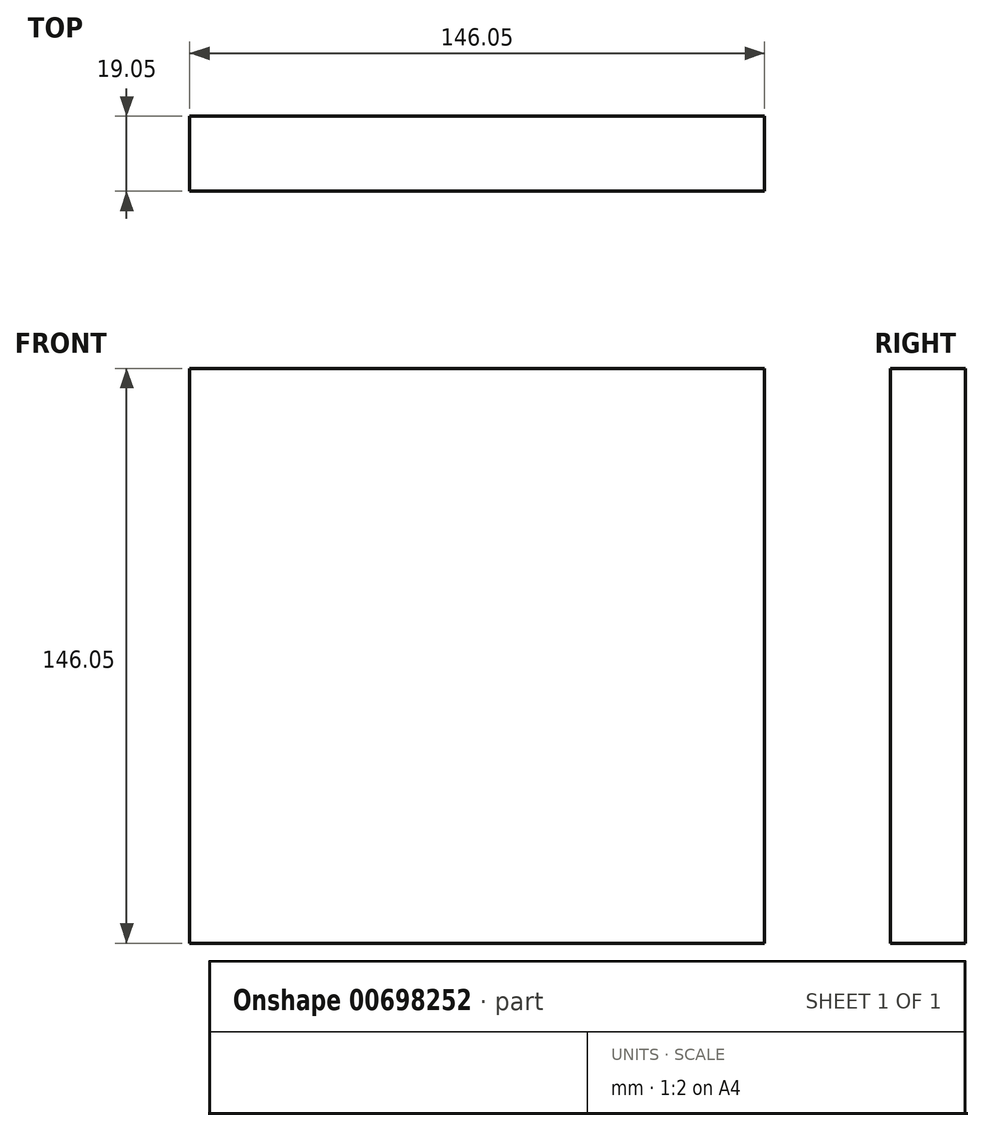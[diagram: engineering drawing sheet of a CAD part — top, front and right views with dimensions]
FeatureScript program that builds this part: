
annotation { "Feature Type Name" : "Feature", "Feature Type Description" : "" }
export const myFeature = defineFeature(function(context is Context, id is Id, definition is map)
    precondition{}
    {
        {
            var Q0;
            Q0=qCreatedBy(makeId("Front.planeOp"),FACE);
            var sketch = newSketch(context, id + "F0", { "sketchPlane" : qUnion([Q0])});
            skLineSegment(sketch, "E0.bottom", {"start": v(-72.42, -55.88) * mm, "end": v(73.63, -55.88) * mm});
            skLineSegment(sketch, "E0.top", {"start": v(-72.42, 90.17) * mm, "end": v(73.63, 90.17) * mm});
            skLineSegment(sketch, "E0.left", {"start": v(-72.42, -55.88) * mm, "end": v(-72.42, 90.17) * mm});
            skLineSegment(sketch, "E0.right", {"start": v(73.63, -55.88) * mm, "end": v(73.63, 90.17) * mm});
            skSolve(sketch);
        }
        {
            var Q0;
            Q0 = qSketchRegion(id + "F0", true);
            extrude(context, id + "F1", {"entities" : qUnion([Q0]), "depth" : 19.05 * mm, "offsetDistance" : 25.4 * mm});
        }
    });
